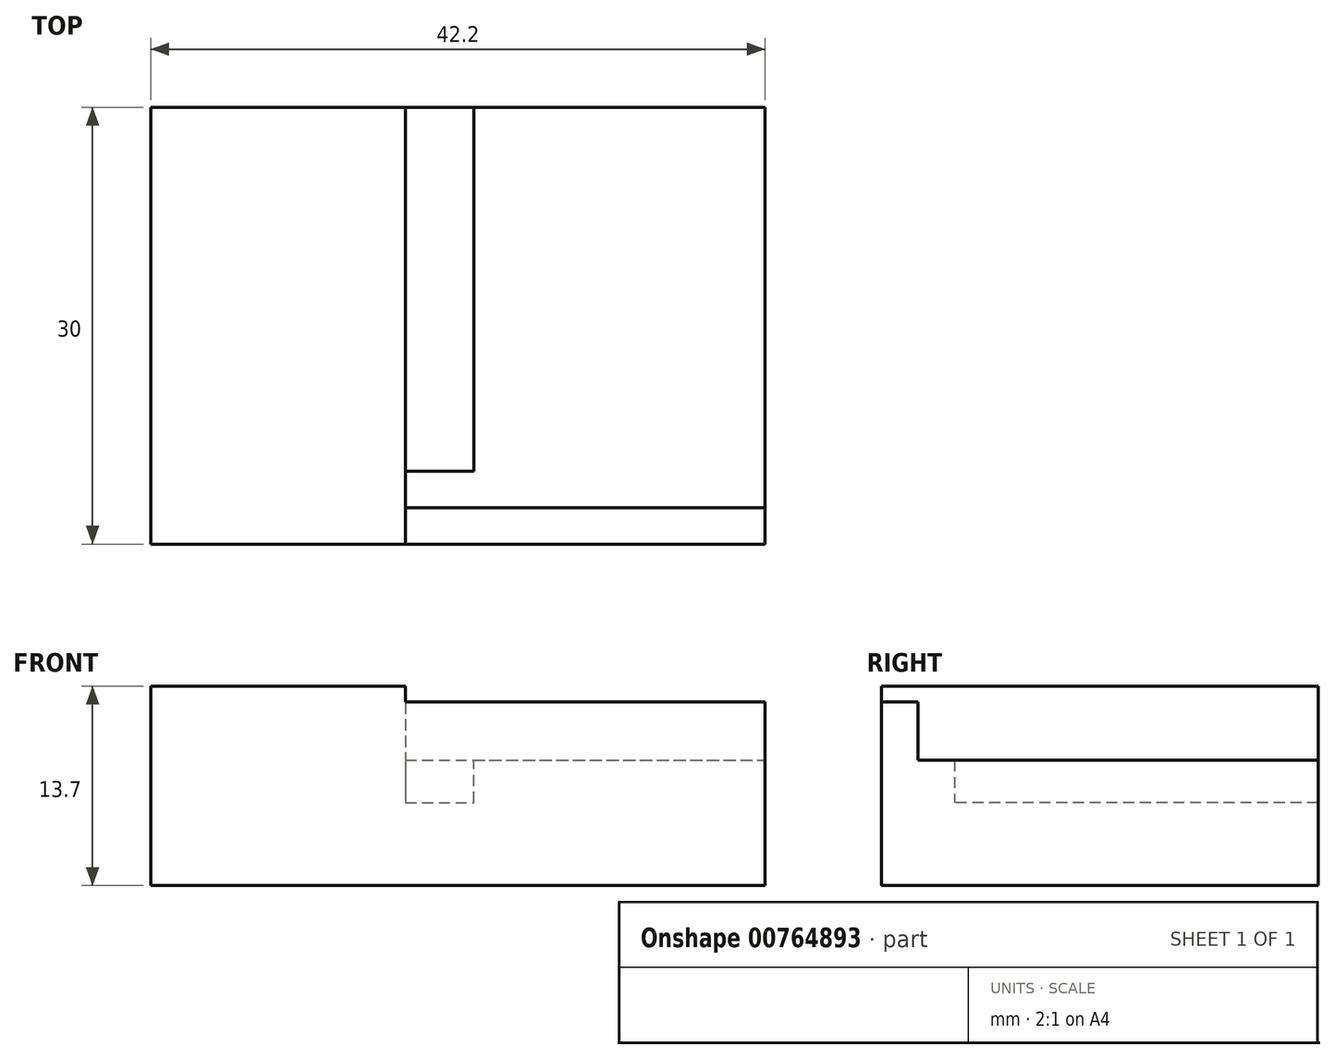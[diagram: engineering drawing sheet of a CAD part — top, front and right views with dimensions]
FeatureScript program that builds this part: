
annotation { "Feature Type Name" : "Feature", "Feature Type Description" : "" }
export const myFeature = defineFeature(function(context is Context, id is Id, definition is map)
    precondition{}
    {
        {
            var Q0;
            Q0=qCreatedBy(makeId("Front.planeOp"),FACE);
            var sketch = newSketch(context, id + "F0", { "sketchPlane" : qUnion([Q0])});
            skLineSegment(sketch, "E0", {"start": v(0, 0) * mm, "end": v(0, 13.7) * mm});
            skLineSegment(sketch, "E1", {"start": v(0, 13.7) * mm, "end": v(17.5, 13.7) * mm});
            skLineSegment(sketch, "E2", {"start": v(17.5, 13.7) * mm, "end": v(17.5, 5.7) * mm});
            skLineSegment(sketch, "E3", {"start": v(17.5, 5.7) * mm, "end": v(22.2, 5.7) * mm});
            skLineSegment(sketch, "E4", {"start": v(22.2, 5.7) * mm, "end": v(22.2, 8.6) * mm});
            skLineSegment(sketch, "E5", {"start": v(17.5, 8.6) * mm, "end": v(42.2, 8.6) * mm});
            skLineSegment(sketch, "E6", {"start": v(42.2, 8.6) * mm, "end": v(42.2, 0) * mm});
            skLineSegment(sketch, "E7", {"start": v(42.2, 0) * mm, "end": v(0, 0) * mm});
            skSolve(sketch);
        }
        {
            var Q0;
            Q0=makeQuery(id+"F0.imprint","IMPRINT",FACE,{"disambiguationData":[TD([[makeQuery(id+"F0.imprint","IMPRINT",EDGE,{"derivedFrom":sQuery(id+"F0.wireOp",EDGE,"E0")}),-1.0]])]});
            extrude(context, id + "F1", {"entities" : qUnion([Q0]), "oppositeDirection" : true, "depth" : 30 * mm, "offsetDistance" : 25 * mm});
        }
        {
            var Q0;
            {var subQ0=sQuery(id+"F0.wireOp",EDGE,"E3");Q0=makeQuery(id+"F0.imprint","IMPRINT",FACE,{"disambiguationData":[TD([[makeQuery(id+"F0.imprint","IMPRINT",EDGE,{"derivedFrom":subQ0}),1.0]])]});}
            extrude(context, id + "F2", {"entities" : qUnion([Q0]), "operationType" : NewBodyOperationType.ADD, "oppositeDirection" : true, "depth" : 5 * mm, "offsetDistance" : 25 * mm});
        }
        {
            var Q0;
            {var subQ0=sQuery(id+"F0.wireOp",EDGE,"E5");Q0=makeQuery(id+"F2.boolean.opBoolean","MERGE",FACE,{"derivedFrom":[makeQuery(id+"F1.opExtrude","SWEPT_FACE",FACE,{"disambiguationData":[OSD([subQ0])]}),makeQuery(id+"F2.opExtrude","SWEPT_FACE",FACE,{"disambiguationData":[OSD([subQ0])]})]});}
            var sketch = newSketch(context, id + "F3", { "sketchPlane" : qUnion([Q0])});
            skLineSegment(sketch, "E8.bottom", {"start": v(17.5, 2.5) * mm, "end": v(42.2, 2.5) * mm});
            skLineSegment(sketch, "E8.top", {"start": v(17.5, 0) * mm, "end": v(42.2, 0) * mm});
            skLineSegment(sketch, "E8.left", {"start": v(17.5, 2.5) * mm, "end": v(17.5, 0) * mm});
            skLineSegment(sketch, "E8.right", {"start": v(42.2, 2.5) * mm, "end": v(42.2, 0) * mm});
            skSolve(sketch);
        }
        {
            var Q0;
            Q0=makeQuery(id+"F3.imprint","IMPRINT",FACE,{"disambiguationData":[TD([[makeQuery(id+"F3.imprint","IMPRINT",EDGE,{"derivedFrom":sQuery(id+"F3.wireOp",EDGE,"E8.top")}),1.0]])]});
            extrude(context, id + "F4", {"entities" : qUnion([Q0]), "operationType" : NewBodyOperationType.ADD, "depth" : 4 * mm, "offsetDistance" : 25 * mm});
        }
    });
